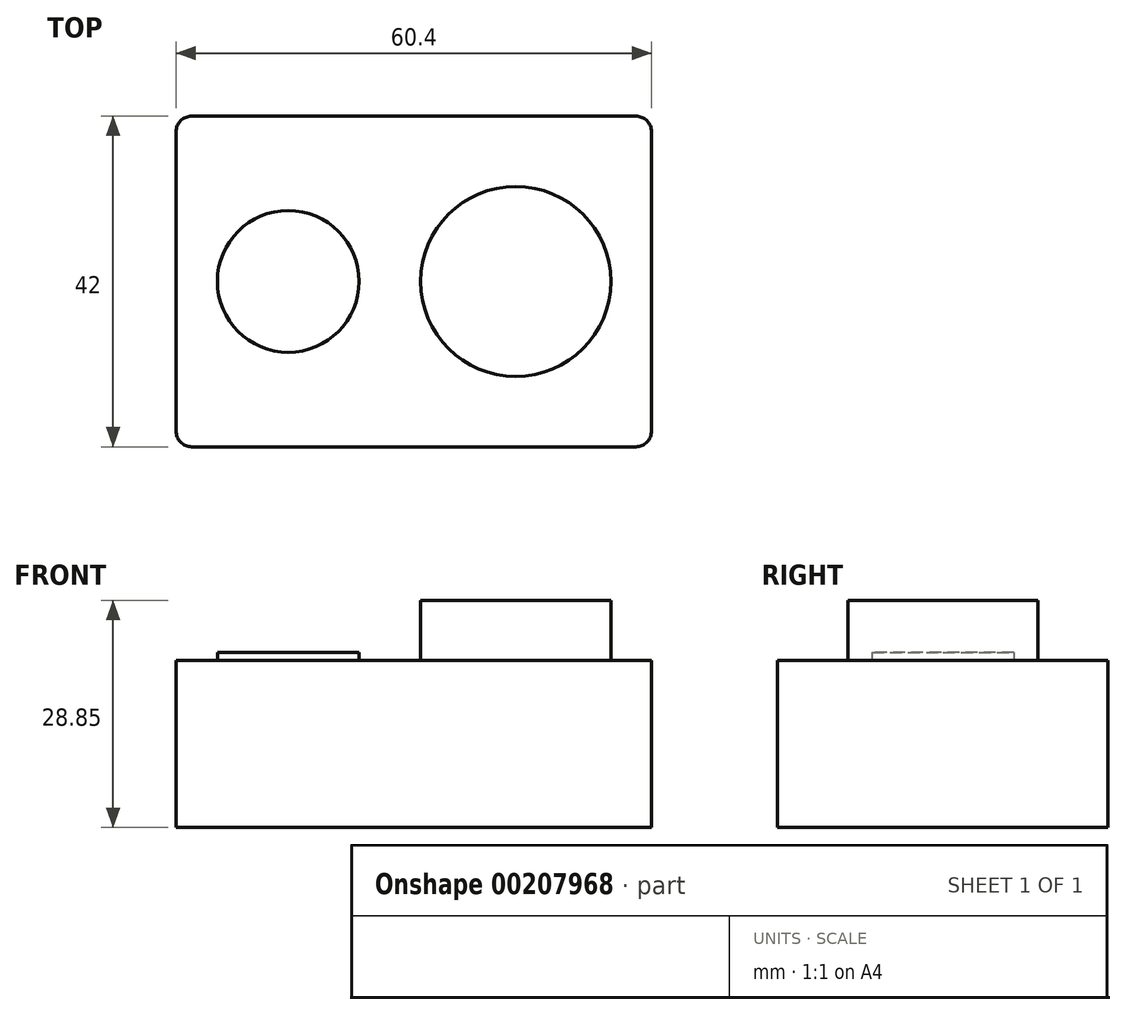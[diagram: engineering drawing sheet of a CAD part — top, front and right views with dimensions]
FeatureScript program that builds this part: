
annotation { "Feature Type Name" : "Feature", "Feature Type Description" : "" }
export const myFeature = defineFeature(function(context is Context, id is Id, definition is map)
    precondition{}
    {
        {
            var Q0;
            Q0=qCreatedBy(makeId("Top.planeOp"),FACE);
            var sketch = newSketch(context, id + "F0", { "sketchPlane" : qUnion([Q0])});
            skLineSegment(sketch, "E0.bottom", {"start": v(-28.2, -21) * mm, "end": v(28.2, -21) * mm});
            skLineSegment(sketch, "E0.top", {"start": v(-28.2, 21) * mm, "end": v(28.2, 21) * mm});
            skLineSegment(sketch, "E0.left", {"start": v(-30.2, -19) * mm, "end": v(-30.2, 19) * mm});
            skLineSegment(sketch, "E0.right", {"start": v(30.2, -19) * mm, "end": v(30.2, 19) * mm});
            skPoint(sketch, "E0.middle", {"position": v(0, 0) * mm});
            skPoint(sketch, "E1.visualSharp", {"position": v(-30.2, 21) * mm});
            skArc(sketch, "E1.filletArc", {"start": v(-28.2, 21) * mm, "mid": v(-29.61, 20.41) * mm, "end": v(-30.2, 19) * mm});
            skPoint(sketch, "E2.visualSharp", {"position": v(-30.2, -21) * mm});
            skArc(sketch, "E2.filletArc", {"start": v(-30.2, -19) * mm, "mid": v(-29.61, -20.41) * mm, "end": v(-28.2, -21) * mm});
            skPoint(sketch, "E3.visualSharp", {"position": v(30.2, -21) * mm});
            skArc(sketch, "E3.filletArc", {"start": v(28.2, -21) * mm, "mid": v(29.61, -20.41) * mm, "end": v(30.2, -19) * mm});
            skPoint(sketch, "E4.visualSharp", {"position": v(30.2, 21) * mm});
            skArc(sketch, "E4.filletArc", {"start": v(30.2, 19) * mm, "mid": v(29.61, 20.41) * mm, "end": v(28.2, 21) * mm});
            skSolve(sketch);
        }
        {
            var Q0;
            Q0=makeQuery(id+"F0.imprint","IMPRINT",FACE,{"disambiguationData":[TD([[makeQuery(id+"F0.imprint","IMPRINT",EDGE,{"derivedFrom":sQuery(id+"F0.wireOp",EDGE,"E0.bottom")}),1.0]])]});
            extrude(context, id + "F1", {"entities" : qUnion([Q0]), "depth" : 21.2 * mm});
        }
        {
            var Q0;
            Q0=makeQuery(id+"F1.opExtrude","CAP_FACE",FACE,{"disambiguationData":[OSD([sQuery(id+"F0.wireOp",EDGE,"E0.bottom"),sQuery(id+"F0.wireOp",EDGE,"E0.top"),sQuery(id+"F0.wireOp",EDGE,"E0.left"),sQuery(id+"F0.wireOp",EDGE,"E0.right"),sQuery(id+"F0.wireOp",EDGE,"E1.filletArc"),sQuery(id+"F0.wireOp",EDGE,"E2.filletArc"),sQuery(id+"F0.wireOp",EDGE,"E3.filletArc"),sQuery(id+"F0.wireOp",EDGE,"E4.filletArc")])],"isStart":false});
            var sketch = newSketch(context, id + "F2", { "sketchPlane" : qUnion([Q0])});
            skCircle(sketch, "E5", {"center": v(-15.95, 0) * mm, "radius": 9 * mm});
            skCircle(sketch, "E6", {"center": v(12.95, 0) * mm, "radius": 13 * mm});
            skCircle(sketch, "E7", {"center": v(12.95, 0) * mm, "radius": 12.07 * mm});
            skSolve(sketch);
        }
        {
            var Q0;
            Q0=makeQuery(id+"F2.imprint","IMPRINT",FACE,{"disambiguationData":[TD([[makeQuery(id+"F2.imprint","IMPRINT",EDGE,{"derivedFrom":sQuery(id+"F2.wireOp",EDGE,"E5")}),1.0]])]});
            extrude(context, id + "F3", {"entities" : qUnion([Q0]), "depth" : 1 * mm});
        }
        {
            var Q0;
            Q0=makeQuery(id+"F1.opExtrude","CAP_FACE",FACE,{"disambiguationData":[OSD([sQuery(id+"F0.wireOp",EDGE,"E0.bottom"),sQuery(id+"F0.wireOp",EDGE,"E0.top"),sQuery(id+"F0.wireOp",EDGE,"E0.left"),sQuery(id+"F0.wireOp",EDGE,"E0.right"),sQuery(id+"F0.wireOp",EDGE,"E1.filletArc"),sQuery(id+"F0.wireOp",EDGE,"E2.filletArc"),sQuery(id+"F0.wireOp",EDGE,"E3.filletArc"),sQuery(id+"F0.wireOp",EDGE,"E4.filletArc")])],"isStart":false});
            var sketch = newSketch(context, id + "F4", { "sketchPlane" : qUnion([Q0])});
            skCircle(sketch, "E8", {"center": v(12.95, 0) * mm, "radius": 13 * mm});
            skCircle(sketch, "E9", {"center": v(12.95, 0) * mm, "radius": 12.07 * mm});
            skSolve(sketch);
        }
        {
            var Q0;
            Q0=makeQuery(id+"F4.imprint","IMPRINT",FACE,{"disambiguationData":[TD([[makeQuery(id+"F4.imprint","IMPRINT",EDGE,{"derivedFrom":sQuery(id+"F4.wireOp",EDGE,"E9")}),1.0]])]});
            extrude(context, id + "F5", {"entities" : qUnion([Q0]), "depth" : 7.65 * mm});
        }
    });
